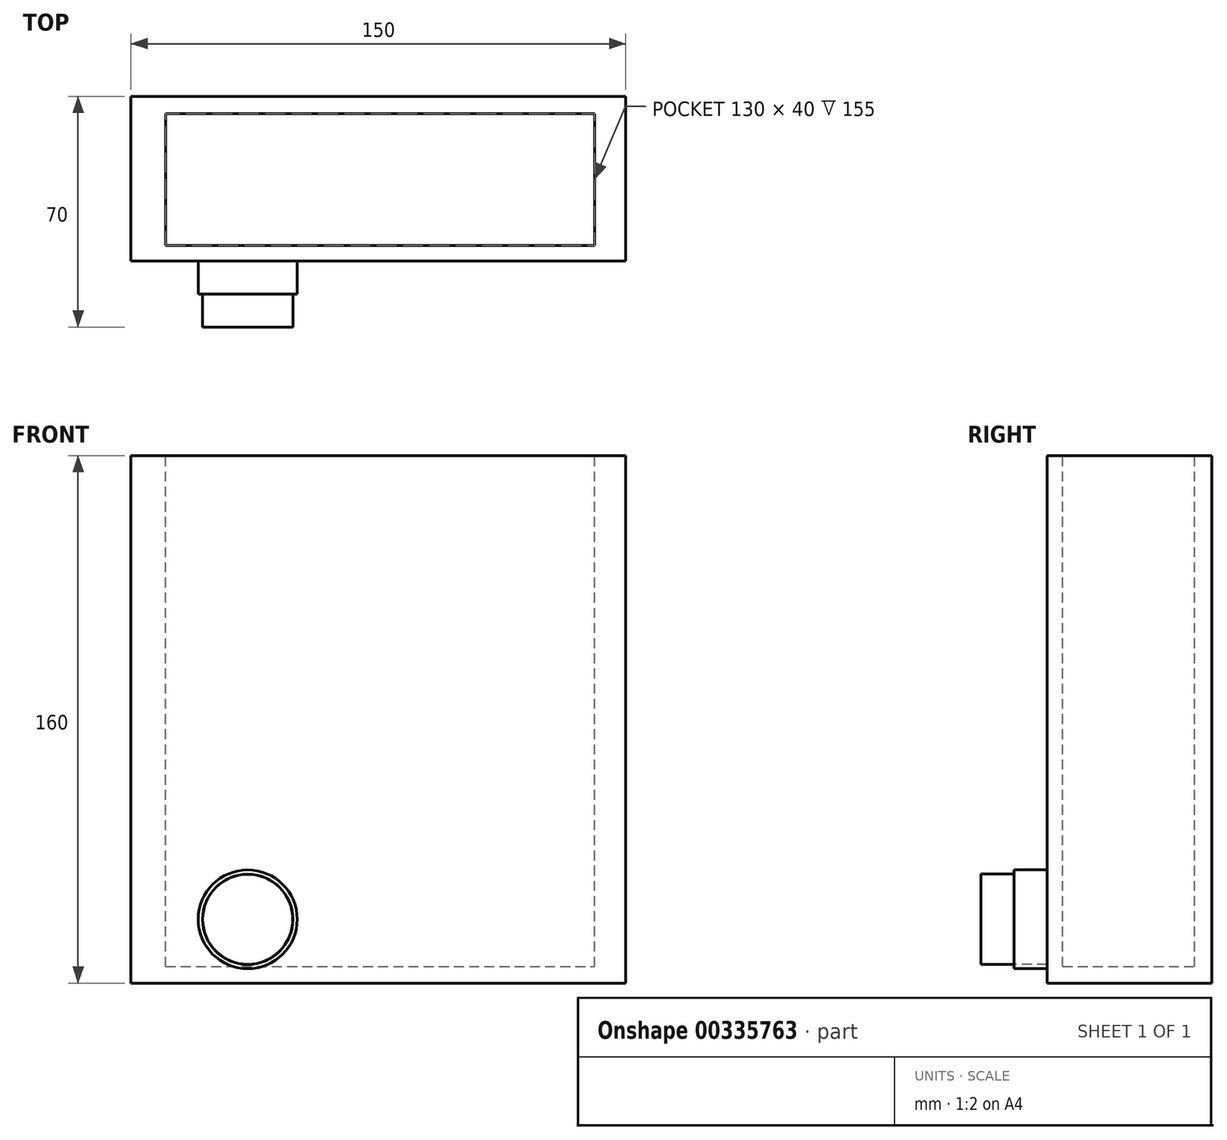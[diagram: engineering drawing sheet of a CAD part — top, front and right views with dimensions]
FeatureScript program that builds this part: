
annotation { "Feature Type Name" : "Feature", "Feature Type Description" : "" }
export const myFeature = defineFeature(function(context is Context, id is Id, definition is map)
    precondition{}
    {
        {
            var Q0;
            Q0=qCreatedBy(makeId("Front.planeOp"),FACE);
            var sketch = newSketch(context, id + "F0", { "sketchPlane" : qUnion([Q0])});
            skLineSegment(sketch, "E0.bottom", {"start": v(-46.07, 76.73) * mm, "end": v(103.93, 76.73) * mm});
            skLineSegment(sketch, "E0.top", {"start": v(-46.07, -83.27) * mm, "end": v(103.93, -83.27) * mm});
            skLineSegment(sketch, "E0.left", {"start": v(-46.07, 76.73) * mm, "end": v(-46.07, -83.27) * mm});
            skLineSegment(sketch, "E0.right", {"start": v(103.93, 76.73) * mm, "end": v(103.93, -83.27) * mm});
            skSolve(sketch);
        }
        {
            var Q0;
            Q0=makeQuery(id+"F0.imprint","IMPRINT",FACE,{"disambiguationData":[TD([[makeQuery(id+"F0.imprint","IMPRINT",EDGE,{"derivedFrom":sQuery(id+"F0.wireOp",EDGE,"E0.bottom")}),-1.0]])]});
            extrude(context, id + "F1", {"entities" : qUnion([Q0]), "depth" : 50 * mm});
        }
        {
            var Q0;
            Q0=makeQuery(id+"F1.opExtrude","SWEPT_FACE",FACE,{"disambiguationData":[OSD([sQuery(id+"F0.wireOp",EDGE,"E0.bottom")])]});
            var sketch = newSketch(context, id + "F2", { "sketchPlane" : qUnion([Q0])});
            skLineSegment(sketch, "E1.bottom", {"start": v(-35.54, -45.27) * mm, "end": v(94.46, -45.27) * mm});
            skLineSegment(sketch, "E1.top", {"start": v(-35.54, -5.27) * mm, "end": v(94.46, -5.27) * mm});
            skLineSegment(sketch, "E1.left", {"start": v(-35.54, -45.27) * mm, "end": v(-35.54, -5.27) * mm});
            skLineSegment(sketch, "E1.right", {"start": v(94.46, -45.27) * mm, "end": v(94.46, -5.27) * mm});
            skSolve(sketch);
        }
        {
            var Q0;
            Q0=makeQuery(id+"F2.imprint","IMPRINT",FACE,{"disambiguationData":[TD([[makeQuery(id+"F2.imprint","IMPRINT",EDGE,{"derivedFrom":sQuery(id+"F2.wireOp",EDGE,"E1.bottom")}),1.0]])]});
            extrude(context, id + "F3", {"entities" : qUnion([Q0]), "operationType" : NewBodyOperationType.REMOVE, "oppositeDirection" : true, "depth" : 155 * mm});
        }
        {
            var Q0;
            Q0=makeQuery(id+"F1.opExtrude","CAP_FACE",FACE,{"disambiguationData":[OSD([sQuery(id+"F0.wireOp",EDGE,"E0.bottom"),sQuery(id+"F0.wireOp",EDGE,"E0.top"),sQuery(id+"F0.wireOp",EDGE,"E0.left"),sQuery(id+"F0.wireOp",EDGE,"E0.right")])],"isStart":false});
            var sketch = newSketch(context, id + "F4", { "sketchPlane" : qUnion([Q0])});
            skCircle(sketch, "E2", {"center": v(-10.68, -63.93) * mm, "radius": 15 * mm});
            skSolve(sketch);
        }
        {
            var Q0;
            Q0=makeQuery(id+"F4.imprint","IMPRINT",FACE,{"disambiguationData":[TD([[makeQuery(id+"F4.imprint","IMPRINT",EDGE,{"derivedFrom":sQuery(id+"F4.wireOp",EDGE,"E2")}),1.0]])]});
            extrude(context, id + "F5", {"entities" : qUnion([Q0]), "operationType" : NewBodyOperationType.ADD, "depth" : 10 * mm});
        }
        {
            var Q0;
            Q0=makeQuery(id+"F5.opExtrude","CAP_FACE",FACE,{"disambiguationData":[OSD([sQuery(id+"F4.wireOp",EDGE,"E2")])],"isStart":false});
            var sketch = newSketch(context, id + "F6", { "sketchPlane" : qUnion([Q0])});
            skCircle(sketch, "E3", {"center": v(-10.68, -63.93) * mm, "radius": 13.7 * mm});
            skSolve(sketch);
        }
        {
            var Q0;
            Q0=makeQuery(id+"F6.imprint","IMPRINT",FACE,{"disambiguationData":[TD([[makeQuery(id+"F6.imprint","IMPRINT",EDGE,{"derivedFrom":sQuery(id+"F6.wireOp",EDGE,"E3")}),1.0]])]});
            extrude(context, id + "F7", {"entities" : qUnion([Q0]), "operationType" : NewBodyOperationType.ADD, "depth" : 10 * mm});
        }
        {
            var Q0;
            Q0=makeQuery(id+"F7.opExtrude","CAP_FACE",FACE,{"disambiguationData":[OSD([sQuery(id+"F6.wireOp",EDGE,"E3")])],"isStart":false});
            var sketch = newSketch(context, id + "F8", { "sketchPlane" : qUnion([Q0])});
            skCircle(sketch, "E4", {"center": v(-10.68, -63.93) * mm, "radius": 13.65 * mm});
            skSolve(sketch);
        }
        {
            var Q0;
            Q0=makeQuery(id+"F8.imprint","IMPRINT",FACE,{"disambiguationData":[TD([[makeQuery(id+"F8.imprint","IMPRINT",EDGE,{"derivedFrom":sQuery(id+"F8.wireOp",EDGE,"E4")}),1.0]])]});
            extrude(context, id + "F9", {"entities" : qUnion([Q0]), "operationType" : NewBodyOperationType.REMOVE, "oppositeDirection" : true, "depth" : 20 * mm});
        }
    });
